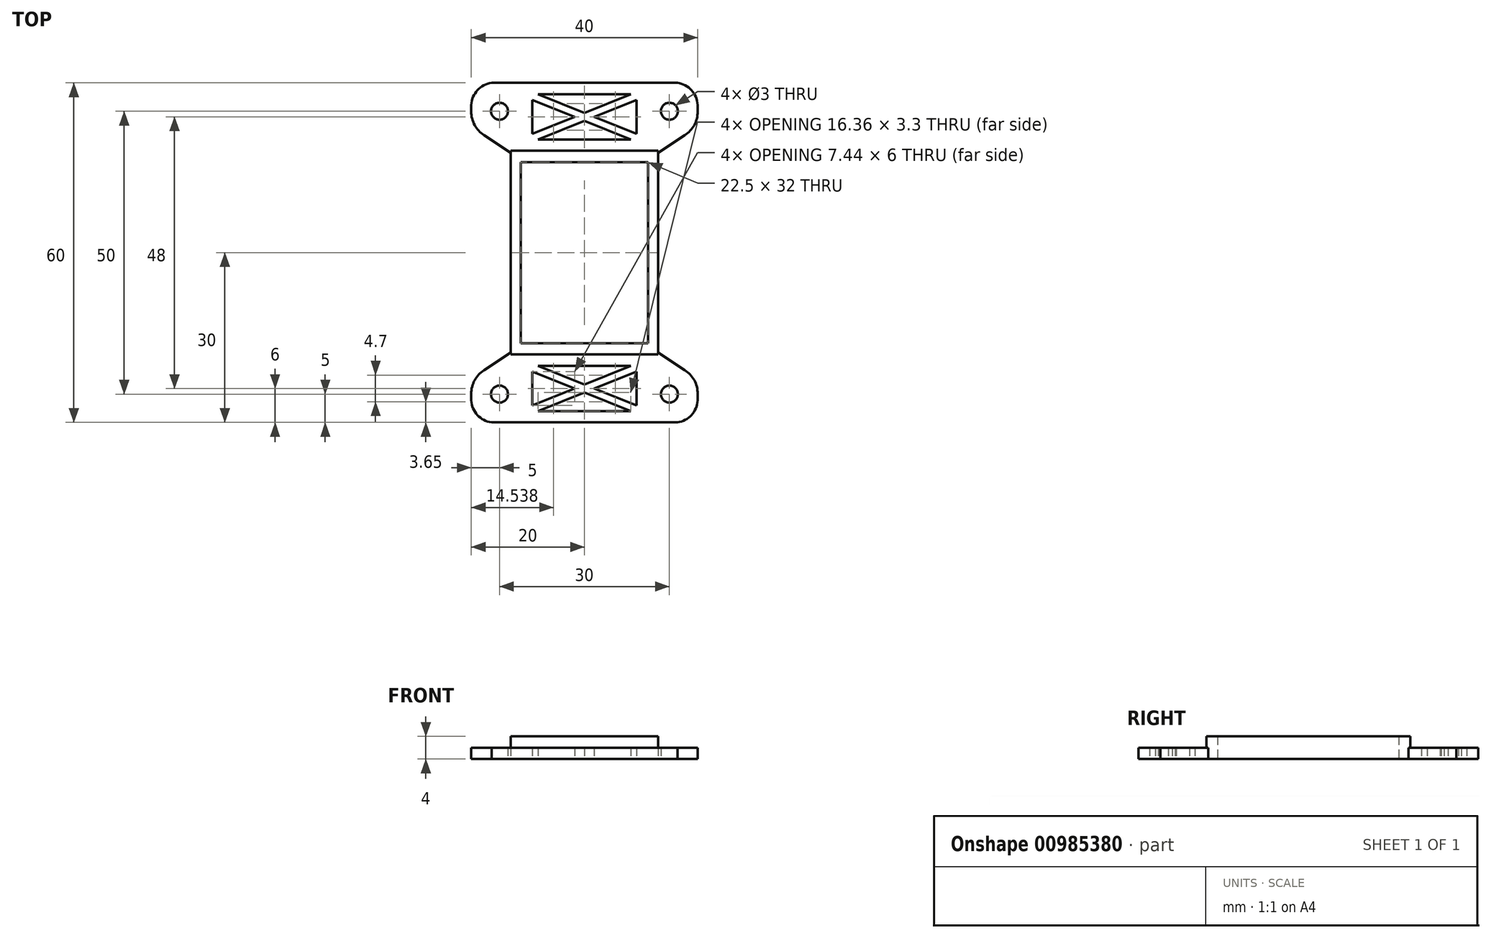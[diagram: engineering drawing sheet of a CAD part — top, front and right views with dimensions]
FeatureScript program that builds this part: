
annotation { "Feature Type Name" : "Feature", "Feature Type Description" : "" }
export const myFeature = defineFeature(function(context is Context, id is Id, definition is map)
    precondition{}
    {
        {
            var Q0;
            Q0=qCreatedBy(makeId("Top.planeOp"),FACE);
            var sketch = newSketch(context, id + "F0", { "sketchPlane" : qUnion([Q0])});
            skLineSegment(sketch, "E0.bottom", {"start": v(16.4, 30) * mm, "end": v(-16.4, 30) * mm});
            skLineSegment(sketch, "E0.top", {"start": v(16.4, -30) * mm, "end": v(-16.4, -30) * mm});
            skLineSegment(sketch, "E0.left", {"start": v(20, 26.11) * mm, "end": v(20, 24.94) * mm});
            skLineSegment(sketch, "E0.right", {"start": v(-20, 26.11) * mm, "end": v(-20, 24.94) * mm});
            skPoint(sketch, "E0.middle", {"position": v(0, 0) * mm});
            skLineSegment(sketch, "E1.bottom", {"start": v(11.25, 16) * mm, "end": v(-11.25, 16) * mm});
            skLineSegment(sketch, "E1.top", {"start": v(11.25, -16) * mm, "end": v(-11.25, -16) * mm});
            skLineSegment(sketch, "E1.left", {"start": v(11.25, 16) * mm, "end": v(11.25, -16) * mm});
            skLineSegment(sketch, "E1.right", {"start": v(-11.25, 16) * mm, "end": v(-11.25, -16) * mm});
            skLineSegment(sketch, "E2.bottom", {"start": v(15, 25) * mm, "end": v(-15, 25) * mm, "construction": true});
            skLineSegment(sketch, "E2.top", {"start": v(15, -25) * mm, "end": v(-15, -25) * mm, "construction": true});
            skLineSegment(sketch, "E2.left", {"start": v(15, 25) * mm, "end": v(15, -25) * mm, "construction": true});
            skLineSegment(sketch, "E2.right", {"start": v(-15, 25) * mm, "end": v(-15, -25) * mm, "construction": true});
            skCircle(sketch, "E3", {"center": v(-15, 25) * mm, "radius": 1.5 * mm});
            skCircle(sketch, "E4", {"center": v(15, 25) * mm, "radius": 1.5 * mm});
            skCircle(sketch, "E5", {"center": v(15, -25) * mm, "radius": 1.5 * mm});
            skCircle(sketch, "E6", {"center": v(-15, -25) * mm, "radius": 1.5 * mm});
            skCircle(sketch, "E7", {"center": v(-15, 25) * mm, "radius": 3.5 * mm});
            skCircle(sketch, "E8", {"center": v(15, 25) * mm, "radius": 3.5 * mm});
            skCircle(sketch, "E9", {"center": v(15, -25) * mm, "radius": 3.5 * mm});
            skCircle(sketch, "E10", {"center": v(-15, -25) * mm, "radius": 3.5 * mm});
            skPoint(sketch, "E11.MirrorCS.end.orphan", {"position": v(-20.41, 25) * mm});
            skPoint(sketch, "E11.MirrorCS.start.orphan", {"position": v(-20, 22.34) * mm});
            skPoint(sketch, "E12.end.orphan", {"position": v(20.41, 25) * mm});
            skPoint(sketch, "E12.start.orphan", {"position": v(20, 22.34) * mm});
            skPoint(sketch, "E13.MirrorCS.end.orphan", {"position": v(20.41, -25) * mm});
            skPoint(sketch, "E13.MirrorCS.start.orphan", {"position": v(20, -22.34) * mm});
            skPoint(sketch, "E14.MirrorCS.end.orphan", {"position": v(-20.41, -25) * mm});
            skPoint(sketch, "E14.MirrorCS.start.orphan", {"position": v(-20, -22.34) * mm});
            skLineSegment(sketch, "E15", {"start": v(-17.73, 20.75) * mm, "end": v(-13, 17.67) * mm});
            skLineSegment(sketch, "E16.MirrorCS", {"start": v(-17.73, -20.75) * mm, "end": v(-13, -17.67) * mm});
            skLineSegment(sketch, "E17.MirrorCS", {"start": v(17.73, -20.75) * mm, "end": v(13, -17.67) * mm});
            skLineSegment(sketch, "E18.MirrorCS", {"start": v(17.73, 20.75) * mm, "end": v(13, 17.67) * mm});
            skLineSegment(sketch, "E19.trimOffspring", {"start": v(20, -24.94) * mm, "end": v(20, -26.11) * mm});
            skLineSegment(sketch, "E20.trimOffspring", {"start": v(-20, -24.94) * mm, "end": v(-20, -26.11) * mm});
            skArc(sketch, "E21", {"start": v(-16.4, 30) * mm, "mid": v(-18.9, 28.7) * mm, "end": v(-20, 26.11) * mm});
            skArc(sketch, "E22.MirrorCS", {"start": v(16.4, 30) * mm, "mid": v(18.9, 28.7) * mm, "end": v(20, 26.11) * mm});
            skArc(sketch, "E23.MirrorCS", {"start": v(16.4, -30) * mm, "mid": v(18.9, -28.7) * mm, "end": v(20, -26.11) * mm});
            skArc(sketch, "E24.MirrorCS", {"start": v(-16.4, -30) * mm, "mid": v(-18.9, -28.7) * mm, "end": v(-20, -26.11) * mm});
            skPoint(sketch, "E25.visualSharp", {"position": v(-20, -22.23) * mm});
            skArc(sketch, "E25.filletArc", {"start": v(-17.73, -20.75) * mm, "mid": v(-19.4, -22.56) * mm, "end": v(-20, -24.94) * mm});
            skPoint(sketch, "E26.visualSharp", {"position": v(20, -22.23) * mm});
            skArc(sketch, "E26.filletArc", {"start": v(20, -24.94) * mm, "mid": v(19.4, -22.56) * mm, "end": v(17.73, -20.75) * mm});
            skPoint(sketch, "E27.visualSharp", {"position": v(20, 22.23) * mm});
            skArc(sketch, "E27.filletArc", {"start": v(17.73, 20.75) * mm, "mid": v(19.4, 22.56) * mm, "end": v(20, 24.94) * mm});
            skPoint(sketch, "E28.visualSharp", {"position": v(-20, 22.23) * mm});
            skArc(sketch, "E28.filletArc", {"start": v(-20, 24.94) * mm, "mid": v(-19.4, 22.56) * mm, "end": v(-17.73, 20.75) * mm});
            skPoint(sketch, "E29.orphan", {"position": v(-20, 30) * mm});
            skPoint(sketch, "E30.orphan", {"position": v(20, 30) * mm});
            skPoint(sketch, "E31.orphan", {"position": v(20, -30) * mm});
            skPoint(sketch, "E32.orphan", {"position": v(-20, -30) * mm});
            skLineSegment(sketch, "E33.bottom", {"start": v(13, 18) * mm, "end": v(-13, 18) * mm});
            skLineSegment(sketch, "E33.top", {"start": v(13, -18) * mm, "end": v(-13, -18) * mm});
            skLineSegment(sketch, "E33.left", {"start": v(13, 18) * mm, "end": v(13, -18) * mm});
            skLineSegment(sketch, "E33.right", {"start": v(-13, 18) * mm, "end": v(-13, -18) * mm});
            skPoint(sketch, "E34.orphan", {"position": v(-11.25, 16.52) * mm});
            skPoint(sketch, "E35.orphan", {"position": v(11.25, 16.52) * mm});
            skPoint(sketch, "E36.orphan", {"position": v(11.25, -16.52) * mm});
            skPoint(sketch, "E37.orphan", {"position": v(-11.25, -16.52) * mm});
            skLineSegment(sketch, "E38.bottom", {"start": v(-9.18, 28) * mm, "end": v(9.17, 28) * mm});
            skLineSegment(sketch, "E38.top", {"start": v(-9.18, 20) * mm, "end": v(9.17, 20) * mm});
            skLineSegment(sketch, "E38.left", {"start": v(-9.18, 28) * mm, "end": v(-9.18, 20) * mm});
            skLineSegment(sketch, "E38.right", {"start": v(9.17, 28) * mm, "end": v(9.17, 20) * mm});
            skLineSegment(sketch, "E39", {"start": v(9.17, 21) * mm, "end": v(1.73, 24) * mm});
            skLineSegment(sketch, "E40", {"start": v(-8.18, 20) * mm, "end": v(0, 23.3) * mm});
            skLineSegment(sketch, "E41.MirrorCS", {"start": v(8.18, 20) * mm, "end": v(0, 23.3) * mm});
            skLineSegment(sketch, "E42.trimOffspring", {"start": v(1.73, 24) * mm, "end": v(9.17, 27) * mm});
            skLineSegment(sketch, "E43.trimOffspring", {"start": v(0, 24.7) * mm, "end": v(-8.18, 28) * mm});
            skLineSegment(sketch, "E44.trimOffspring", {"start": v(0, 24.7) * mm, "end": v(8.18, 28) * mm});
            skLineSegment(sketch, "E45", {"start": v(-9.18, 21) * mm, "end": v(-1.74, 24) * mm});
            skLineSegment(sketch, "E46", {"start": v(-1.74, 24) * mm, "end": v(-9.18, 27) * mm});
            skLineSegment(sketch, "E47.MirrorCS", {"start": v(8.18, -20) * mm, "end": v(0, -23.3) * mm});
            skLineSegment(sketch, "E48.MirrorCS", {"start": v(9.17, -21) * mm, "end": v(1.73, -24) * mm});
            skLineSegment(sketch, "E49.MirrorCS", {"start": v(1.73, -24) * mm, "end": v(9.17, -27) * mm});
            skLineSegment(sketch, "E50.MirrorCS", {"start": v(0, -24.7) * mm, "end": v(8.18, -28) * mm});
            skLineSegment(sketch, "E51.MirrorCS", {"start": v(0, -24.7) * mm, "end": v(-8.18, -28) * mm});
            skLineSegment(sketch, "E52.MirrorCS", {"start": v(-1.74, -24) * mm, "end": v(-9.18, -27) * mm});
            skLineSegment(sketch, "E53.MirrorCS", {"start": v(-8.18, -20) * mm, "end": v(0, -23.3) * mm});
            skLineSegment(sketch, "E54.MirrorCS", {"start": v(-9.18, -21) * mm, "end": v(-1.74, -24) * mm});
            skLineSegment(sketch, "E55.MirrorCS", {"start": v(9.17, -28) * mm, "end": v(9.17, -20) * mm});
            skLineSegment(sketch, "E56.MirrorCS", {"start": v(-9.18, -20) * mm, "end": v(9.17, -20) * mm});
            skLineSegment(sketch, "E57.MirrorCS", {"start": v(-9.18, -28) * mm, "end": v(-9.18, -20) * mm});
            skLineSegment(sketch, "E58.MirrorCS", {"start": v(-9.18, -28) * mm, "end": v(9.17, -28) * mm});
            skSolve(sketch);
        }
        {
            var Q0;
            Q0=makeQuery(id+"F0.imprint","IMPRINT",FACE,{"disambiguationData":[TD([[makeQuery(id+"F0.imprint","IMPRINT",EDGE,{"derivedFrom":sQuery(id+"F0.wireOp",EDGE,"E0.bottom")}),1.0]])]});
            var Q1;
            Q1=makeQuery(id+"F0.imprint","IMPRINT",FACE,{"disambiguationData":[TD([[makeQuery(id+"F0.imprint","IMPRINT",EDGE,{"derivedFrom":sQuery(id+"F0.wireOp",EDGE,"E0.top")}),-1.0]])]});
            var Q2;
            Q2=makeQuery(id+"F0.imprint","IMPRINT",FACE,{"disambiguationData":[TD([[makeQuery(id+"F0.imprint","IMPRINT",EDGE,{"derivedFrom":sQuery(id+"F0.wireOp",EDGE,"E6")}),-1.0]])]});
            var Q3;
            Q3=makeQuery(id+"F0.imprint","IMPRINT",FACE,{"disambiguationData":[TD([[makeQuery(id+"F0.imprint","IMPRINT",EDGE,{"derivedFrom":sQuery(id+"F0.wireOp",EDGE,"E5")}),-1.0]])]});
            var Q4;
            Q4=makeQuery(id+"F0.imprint","IMPRINT",FACE,{"disambiguationData":[TD([[makeQuery(id+"F0.imprint","IMPRINT",EDGE,{"derivedFrom":sQuery(id+"F0.wireOp",EDGE,"E4")}),-1.0]])]});
            var Q5;
            Q5=makeQuery(id+"F0.imprint","IMPRINT",FACE,{"disambiguationData":[TD([[makeQuery(id+"F0.imprint","IMPRINT",EDGE,{"derivedFrom":sQuery(id+"F0.wireOp",EDGE,"E3")}),-1.0]])]});
            var Q6;
            {var subQ0=sQuery(id+"F0.wireOp",EDGE,"E40");Q6=makeQuery(id+"F0.imprint","IMPRINT",FACE,{"disambiguationData":[TD([[makeQuery(id+"F0.imprint","IMPRINT",EDGE,{"derivedFrom":subQ0}),1.0]])]});}
            var Q7;
            {var subQ11=sQuery(id+"F0.wireOp",EDGE,"E47.MirrorCS");Q7=makeQuery(id+"F0.imprint","IMPRINT",FACE,{"disambiguationData":[TD([[makeQuery(id+"F0.imprint","IMPRINT",EDGE,{"derivedFrom":subQ11}),1.0]])]});}
            extrude(context, id + "F1", {"entities" : qUnion([Q0, Q1, Q2, Q3, Q4, Q5, Q6, Q7]), "depth" : 2 * mm, "offsetDistance" : 25 * mm});
        }
        {
            var Q0;
            Q0=makeQuery(id+"F0.imprint","IMPRINT",FACE,{"disambiguationData":[TD([[makeQuery(id+"F0.imprint","IMPRINT",EDGE,{"derivedFrom":sQuery(id+"F0.wireOp",EDGE,"E1.bottom")}),-1.0]])]});
            extrude(context, id + "F2", {"entities" : qUnion([Q0]), "operationType" : NewBodyOperationType.ADD, "depth" : 4 * mm, "offsetDistance" : 25 * mm});
        }
    });
